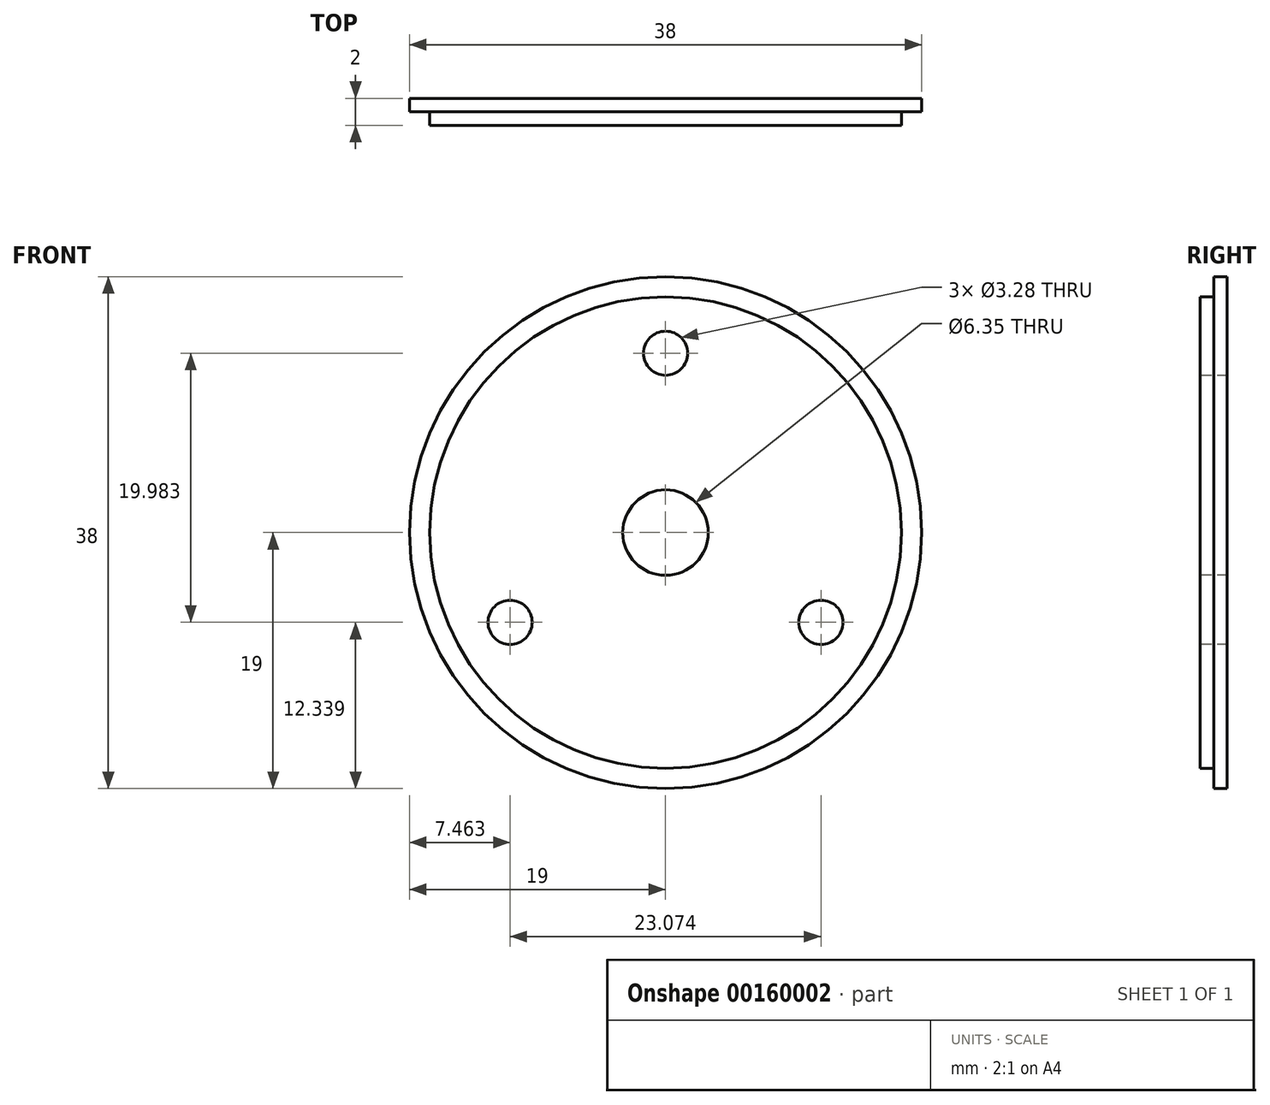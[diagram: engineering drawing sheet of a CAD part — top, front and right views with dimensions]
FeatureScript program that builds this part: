
annotation { "Feature Type Name" : "Feature", "Feature Type Description" : "" }
export const myFeature = defineFeature(function(context is Context, id is Id, definition is map)
    precondition{}
    {
        {
            var Q0;
            Q0=qCreatedBy(makeId("Front.planeOp"),FACE);
            var sketch = newSketch(context, id + "F0", { "sketchPlane" : qUnion([Q0])});
            skCircle(sketch, "E0", {"center": v(0, 0) * mm, "radius": 17.5 * mm});
            skSolve(sketch);
        }
        {
            var Q0;
            Q0 = qSketchRegion(id + "F0", true);
            extrude(context, id + "F1", {"entities" : qUnion([Q0]), "depth" : 1 * mm});
        }
        {
            var Q0;
            Q0=makeQuery(id+"F1.opExtrude","CAP_FACE",FACE,{"disambiguationData":[OSD([sQuery(id+"F0.wireOp",EDGE,"E0")])],"isStart":true});
            var sketch = newSketch(context, id + "F2", { "sketchPlane" : qUnion([Q0])});
            skCircle(sketch, "E1", {"center": v(0, 0) * mm, "radius": 19 * mm});
            skSolve(sketch);
        }
        {
            var Q0;
            Q0 = qSketchRegion(id + "F2", true);
            extrude(context, id + "F3", {"entities" : qUnion([Q0]), "operationType" : NewBodyOperationType.ADD, "depth" : 1 * mm});
        }
        {
            var Q0;
            Q0=makeQuery(id+"F1.opExtrude","CAP_FACE",FACE,{"disambiguationData":[OSD([sQuery(id+"F0.wireOp",EDGE,"E0")])],"isStart":false});
            var sketch = newSketch(context, id + "F4", { "sketchPlane" : qUnion([Q0])});
            skCircle(sketch, "E2", {"center": v(0, 0) * mm, "radius": 3.18 * mm});
            skSolve(sketch);
        }
        {
            var Q0;
            Q0 = qSketchRegion(id + "F4", true);
            extrude(context, id + "F5", {"entities" : qUnion([Q0]), "operationType" : NewBodyOperationType.REMOVE, "oppositeDirection" : true, "depth" : 25.4 * mm});
        }
        {
            var Q0;
            Q0=makeQuery(id+"F1.opExtrude","CAP_FACE",FACE,{"disambiguationData":[OSD([sQuery(id+"F0.wireOp",EDGE,"E0")])],"isStart":false});
            var sketch = newSketch(context, id + "F6", { "sketchPlane" : qUnion([Q0])});
            skCircle(sketch, "E3", {"center": v(0, 13.32) * mm, "radius": 1.64 * mm});
            skCircle(sketch, "E4.1.0", {"center": v(-11.54, -6.66) * mm, "radius": 1.64 * mm});
            skCircle(sketch, "E4.2.0", {"center": v(11.54, -6.66) * mm, "radius": 1.64 * mm});
            skPoint(sketch, "E4.center", {"position": v(0, 0) * mm});
            skSolve(sketch);
        }
        {
            var Q0;
            Q0 = qSketchRegion(id + "F6", true);
            extrude(context, id + "F7", {"entities" : qUnion([Q0]), "operationType" : NewBodyOperationType.REMOVE, "oppositeDirection" : true, "depth" : 25.4 * mm});
        }
    });
